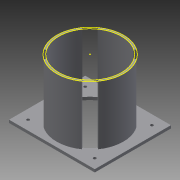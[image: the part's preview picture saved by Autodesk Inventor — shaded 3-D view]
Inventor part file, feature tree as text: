
AUTODESK INVENTOR PART (.ipt)
format: ipt  version: 2013 (Build 170138000, 138)  size: 144,896 bytes
history: native  units: mm
features: sketch x6, extrude x4, other x1, hole x1
ambient origin geometry x8: Origin, YZ Plane, XZ Plane, XY Plane, X Axis, Y Axis, Z Axis, Center Point
feature tree (12):
  other  "ソリッド1"
  extrude  "押し出し1"  Depth=70.0mm
  extrude  "押し出し2"  Depth=66.0mm
  extrude  "押し出し3"  Depth=90.0mm
  sketch  "スケッチ4"
  hole  "穴1"  [1 undecoded]
  extrude  "押し出し4"  Depth=3.0mm TaperAngle=0.0deg
  sketch  "スケッチ1"
  sketch  "スケッチ2"
  sketch  "スケッチ3"
  sketch  "スケッチ5"
  sketch  "スケッチ6"
note: 1 required parameter value undecoded (feature->parameter linkage not recoverable at this tier; creation-order binding heuristic only, values carry confidence <= 0.55)
